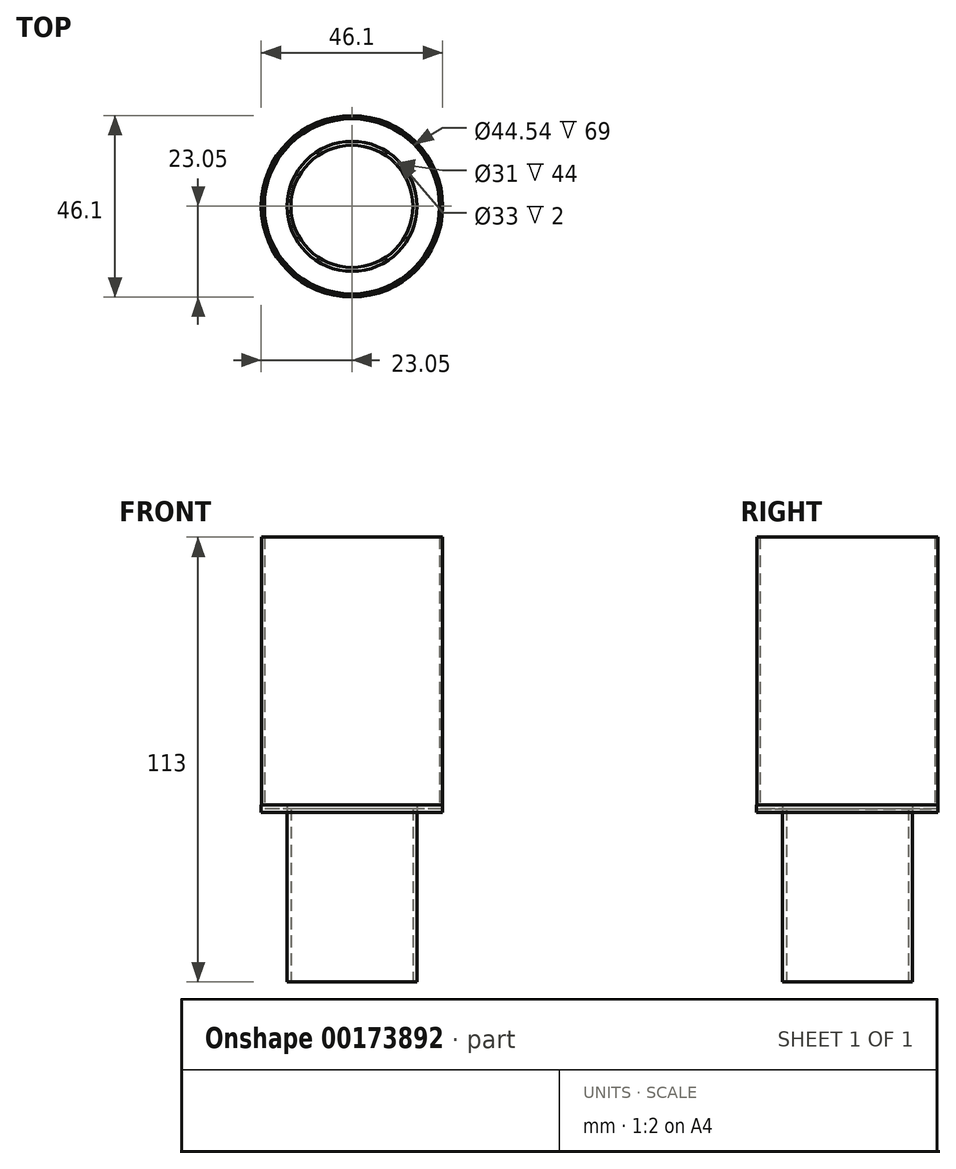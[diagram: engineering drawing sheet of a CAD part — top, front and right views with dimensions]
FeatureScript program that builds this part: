
annotation { "Feature Type Name" : "Feature", "Feature Type Description" : "" }
export const myFeature = defineFeature(function(context is Context, id is Id, definition is map)
    precondition{}
    {
        {
            var Q0;
            Q0=qCreatedBy(makeId("Top.planeOp"),FACE);
            var sketch = newSketch(context, id + "F0", { "sketchPlane" : qUnion([Q0])});
            skCircle(sketch, "E0", {"center": v(0, 0) * mm, "radius": 15.5 * mm});
            skCircle(sketch, "E1", {"center": v(0, 0) * mm, "radius": 16.5 * mm});
            skSolve(sketch);
        }
        {
            var Q0;
            Q0=makeQuery(id+"F0.imprint","IMPRINT",FACE,{"disambiguationData":[TD([[makeQuery(id+"F0.imprint","IMPRINT",EDGE,{"derivedFrom":sQuery(id+"F0.wireOp",EDGE,"E0")}),-1.0]])]});
            extrude(context, id + "F1", {"entities" : qUnion([Q0]), "depth" : 44 * mm});
        }
        {
            var Q0;
            Q0=makeQuery(id+"F1.opExtrude","CAP_FACE",FACE,{"disambiguationData":[OSD([sQuery(id+"F0.wireOp",EDGE,"E0"),sQuery(id+"F0.wireOp",EDGE,"E1")])],"isStart":false});
            var sketch = newSketch(context, id + "F2", { "sketchPlane" : qUnion([Q0])});
            skCircle(sketch, "E2", {"center": v(0, 0) * mm, "radius": 23 * mm});
            skCircle(sketch, "E3", {"center": v(0, 0) * mm, "radius": 22.27 * mm});
            skSolve(sketch);
        }
        {
            var Q0;
            Q0 = qSketchRegion(id + "F2", true);
            extrude(context, id + "F3", {"entities" : qUnion([Q0]), "depth" : 25 * mm});
        }
        {
            var Q0;
            Q0=makeQuery(id+"F3.opExtrude","CAP_FACE",FACE,{"disambiguationData":[OSD([sQuery(id+"F2.wireOp",EDGE,"E2"),sQuery(id+"F2.wireOp",EDGE,"E3")])],"isStart":false});
            extrude(context, id + "F4", {"entities" : qUnion([Q0]), "operationType" : NewBodyOperationType.ADD, "depth" : 44 * mm});
        }
        {
            var Q0;
            Q0=makeQuery(id+"F1.opExtrude","CAP_FACE",FACE,{"disambiguationData":[OSD([sQuery(id+"F0.wireOp",EDGE,"E0"),sQuery(id+"F0.wireOp",EDGE,"E1")])],"isStart":false});
            var sketch = newSketch(context, id + "F5", { "sketchPlane" : qUnion([Q0])});
            skCircle(sketch, "E4", {"center": v(0, 0) * mm, "radius": 15.46 * mm});
            skCircle(sketch, "E5", {"center": v(0, 0) * mm, "radius": 23.05 * mm});
            skSolve(sketch);
        }
        {
            var Q0;
            Q0=makeQuery(id+"F5.imprint","IMPRINT",FACE,{"disambiguationData":[TD([[makeQuery(id+"F5.imprint","IMPRINT",EDGE,{"derivedFrom":sQuery(id+"F5.wireOp",EDGE,"E5")}),1.0]])]});
            extrude(context, id + "F6", {"entities" : qUnion([Q0]), "endBound" : BoundingType.SYMMETRIC, "depth" : 2 * mm});
        }
    });
